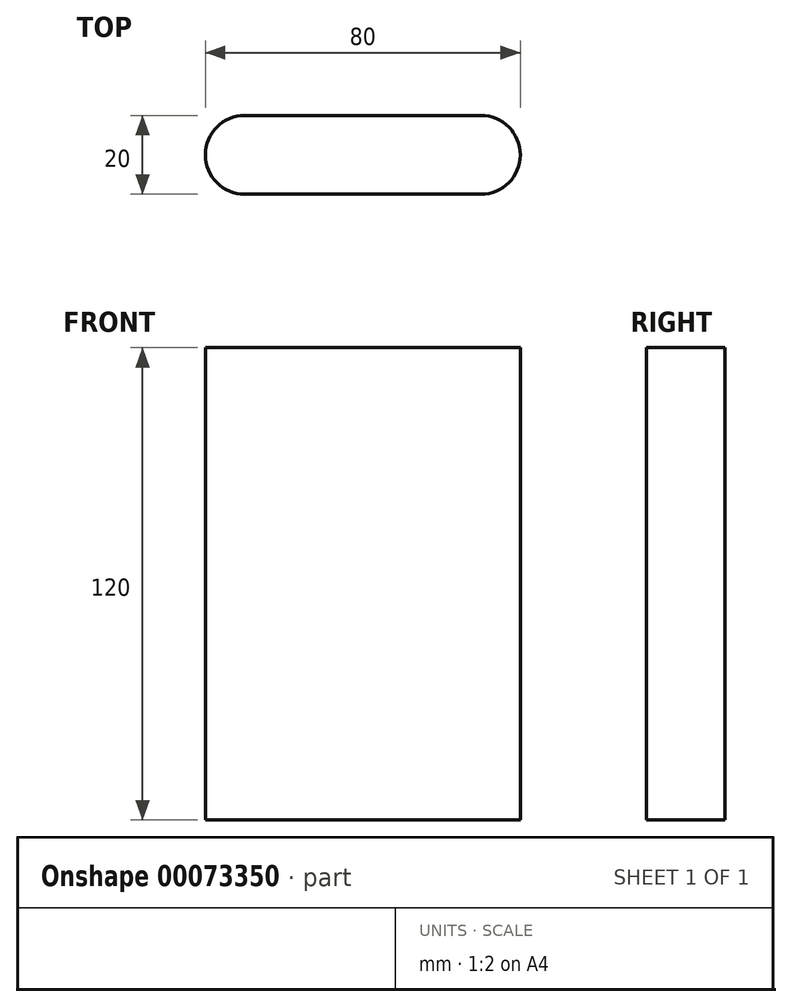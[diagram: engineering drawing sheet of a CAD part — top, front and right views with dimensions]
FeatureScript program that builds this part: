
annotation { "Feature Type Name" : "Feature", "Feature Type Description" : "" }
export const myFeature = defineFeature(function(context is Context, id is Id, definition is map)
    precondition{}
    {
        {
            var Q0;
            Q0=qCreatedBy(makeId("Top.planeOp"),FACE);
            var sketch = newSketch(context, id + "F0", { "sketchPlane" : qUnion([Q0])});
            skLineSegment(sketch, "E0.bottom", {"start": v(-30, 10) * mm, "end": v(30, 10) * mm});
            skLineSegment(sketch, "E0.top", {"start": v(-30, -10) * mm, "end": v(30, -10) * mm});
            skLineSegment(sketch, "E0.left", {"start": v(-30, 10) * mm, "end": v(-30, -10) * mm});
            skLineSegment(sketch, "E0.right", {"start": v(30, 10) * mm, "end": v(30, -10) * mm});
            skLineSegment(sketch, "E1", {"start": v(-30, 0) * mm, "end": v(30, 0) * mm});
            skPoint(sketch, "E2", {"position": v(0, 0) * mm});
            skCircle(sketch, "E3", {"center": v(-30, 0) * mm, "radius": 10 * mm});
            skCircle(sketch, "E4", {"center": v(30, 0) * mm, "radius": 10 * mm});
            skSolve(sketch);
        }
        {
            var Q0;
            Q0 = qSketchRegion(id + "F0", true);
            extrude(context, id + "F1", {"entities" : qUnion([Q0]), "depth" : 120 * mm, "symmetric" : true});
        }
    });
